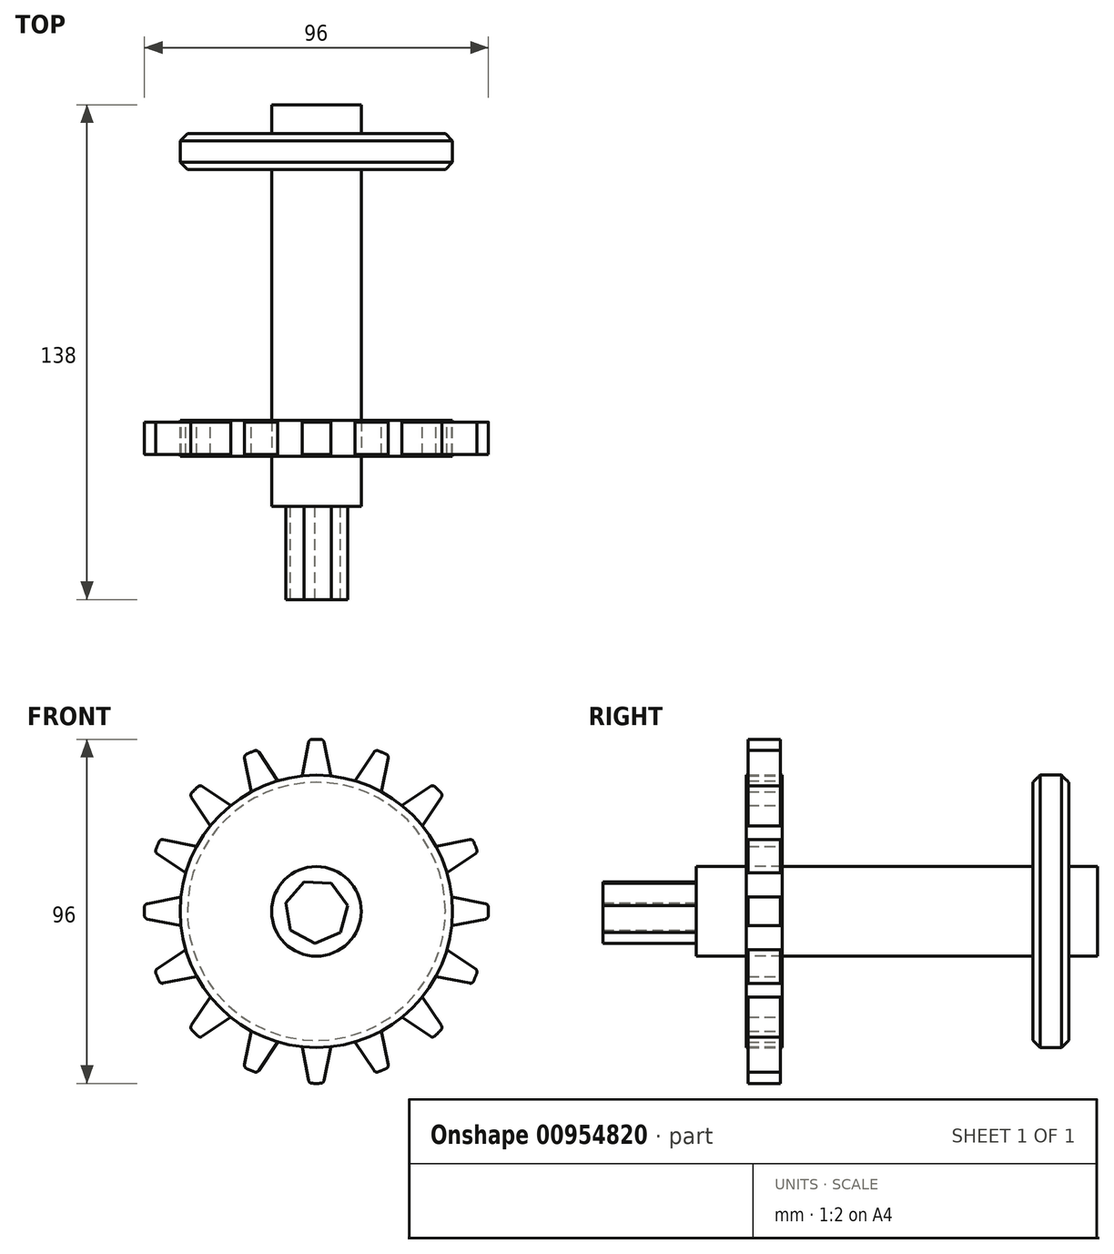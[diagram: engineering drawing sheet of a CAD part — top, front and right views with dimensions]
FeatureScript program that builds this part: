
annotation { "Feature Type Name" : "Feature", "Feature Type Description" : "" }
export const myFeature = defineFeature(function(context is Context, id is Id, definition is map)
    precondition{}
    {
        {
            var Q0;
            Q0=qCreatedBy(makeId("Front.planeOp"),FACE);
            var sketch = newSketch(context, id + "F0", { "sketchPlane" : qUnion([Q0])});
            skCircle(sketch, "E0", {"center": v(0, 0) * mm, "radius": 38 * mm});
            skSolve(sketch);
        }
        {
            var Q0;
            Q0=qSketchRegion(id+"F0",true);
            extrude(context, id + "F1", {"entities" : qUnion([Q0]), "depth" : 10 * mm, "offsetDistance" : 25 * mm});
        }
        {
            var Q0;
            Q0=qCreatedBy(makeId("Front.planeOp"),FACE);
            var Q1;
            Q1=makeQuery(id+"F1.opExtrude","CAP_FACE",FACE,{"disambiguationData":[OSD([sQuery(id+"F0.wireOp",EDGE,"E0")])],"isStart":false});
            cPlane(context, id + "F2", {"entities" : qUnion([Q0, Q1]), "cplaneType" : CPlaneType.MID_PLANE, "offset" : 25 * mm, "width" : 150 * mm, "height" : 150 * mm});
        }
        {
            var Q0;
            Q0=qCreatedBy(id+"F2.planeOp",FACE);
            var sketch = newSketch(context, id + "F3", { "sketchPlane" : qUnion([Q0])});
            skLineSegment(sketch, "E1", {"start": v(-37.79, -4) * mm, "end": v(-37.79, 4) * mm});
            skPoint(sketch, "E2.end.orphan", {"position": v(30.14, 4) * mm});
            skPoint(sketch, "E2.start.orphan", {"position": v(29.89, 0) * mm});
            skLineSegment(sketch, "E3", {"start": v(-37.79, 4) * mm, "end": v(-47.96, 2) * mm});
            skLineSegment(sketch, "E4", {"start": v(-37.79, -4) * mm, "end": v(-47.96, -2) * mm});
            skArc(sketch, "E5", {"start": v(-47.96, 2) * mm, "mid": v(-48, 0) * mm, "end": v(-47.96, -2) * mm, "construction": true});
            skArc(sketch, "E6", {"start": v(-47.96, 2) * mm, "mid": v(-48, 0) * mm, "end": v(-47.96, -2) * mm});
            skSolve(sketch);
        }
        {
            var Q0;
            Q0=makeQuery(id+"F3.imprint","IMPRINT",FACE,{"disambiguationData":[TD([[makeQuery(id+"F3.imprint","IMPRINT",EDGE,{"derivedFrom":sQuery(id+"F3.wireOp",EDGE,"E1")}),1.0]])]});
            extrude(context, id + "F4", {"entities" : qUnion([Q0]), "operationType" : NewBodyOperationType.ADD, "depth" : 9 * mm, "offsetDistance" : 25 * mm, "symmetric" : true});
        }
        {
            var Q0;
            Q0=makeQuery(id+"F4.opExtrude","SWEPT_EDGE",EDGE,{"disambiguationData":[OSD([sQuery(id+"F3.wireOp",EDGE,"E4"),sQuery(id+"F3.wireOp",EDGE,"E6")])]});
            var Q1;
            Q1=makeQuery(id+"F4.opExtrude","SWEPT_EDGE",EDGE,{"disambiguationData":[OSD([sQuery(id+"F3.wireOp",EDGE,"E3"),sQuery(id+"F3.wireOp",EDGE,"E6")])]});
            fillet(context, id + "F5", {"entities" : qUnion([Q0, Q1]), "radius" : 1 * mm, "tangentPropagation" : true, "allowEdgeOverflow" : false});
        }
        {
            var Q0;
            Q0=makeQuery(id+"F1.opExtrude","SWEPT_BODY",BODY,{"disambiguationData":[OSD([sQuery(id+"F0.wireOp",EDGE,"E0")])]});
            var Q1;
            Q1=makeQuery(id+"F1.opExtrude","CAP_EDGE",EDGE,{"disambiguationData":[OSD([sQuery(id+"F0.wireOp",EDGE,"E0")])],"isStart":true});
            circularPattern(context, id + "F6", {"entities" : qUnion([Q0]), "axis" : qUnion([Q1]), "angle" : 360 * degree, "instanceCount" : 16, "equalSpace" : true});
        }
        {
            var Q0;
            Q0=makeQuery(id+"F1.opExtrude","CAP_FACE",FACE,{"disambiguationData":[OSD([sQuery(id+"F0.wireOp",EDGE,"E0")])],"isStart":false});
            var sketch = newSketch(context, id + "F7", { "sketchPlane" : qUnion([Q0])});
            skCircle(sketch, "E7", {"center": v(0, 0) * mm, "radius": 12.5 * mm});
            skPoint(sketch, "E8.0.midPoint", {"position": v(7.03, 3.82) * mm});
            skPoint(sketch, "E9.orphan", {"position": v(4.82, 7.88) * mm});
            skPoint(sketch, "E8.0.end.orphan", {"position": v(9.23, -0.24) * mm});
            skSolve(sketch);
        }
        {
            var Q0;
            Q0 = qSketchRegion(id + "F7", true);
            extrude(context, id + "F8", {"entities" : qUnion([Q0]), "oppositeDirection" : true, "depth" : 98 * mm, "offsetDistance" : 25 * mm});
        }
        {
            var Q0;
            Q0=makeQuery(id+"F8.opExtrude","CAP_FACE",FACE,{"disambiguationData":[OSD([sQuery(id+"F7.wireOp",EDGE,"E7")])],"isStart":true});
            extrude(context, id + "F9", {"entities" : qUnion([Q0]), "depth" : 14 * mm, "offsetDistance" : 25 * mm});
        }
        {
            var Q0;
            Q0=makeQuery(id+"F9.opExtrude","CAP_FACE",FACE,{"disambiguationData":[OSD([sQuery(id+"F7.wireOp",EDGE,"E7")])],"isStart":false});
            var sketch = newSketch(context, id + "F10", { "sketchPlane" : qUnion([Q0])});
            skCircle(sketch, "E10.cCircle", {"center": v(0, 0) * mm, "radius": 8 * mm, "construction": true});
            skLineSegment(sketch, "E10.0", {"start": v(4.23, 7.8) * mm, "end": v(8.74, 1.57) * mm});
            skLineSegment(sketch, "E10.1", {"start": v(8.74, 1.57) * mm, "end": v(6.67, -5.86) * mm});
            skLineSegment(sketch, "E10.2", {"start": v(6.67, -5.86) * mm, "end": v(-0.42, -8.87) * mm});
            skLineSegment(sketch, "E10.3", {"start": v(-0.42, -8.87) * mm, "end": v(-7.2, -5.2) * mm});
            skLineSegment(sketch, "E10.4", {"start": v(-7.2, -5.2) * mm, "end": v(-8.55, 2.38) * mm});
            skLineSegment(sketch, "E10.5", {"start": v(-8.55, 2.38) * mm, "end": v(-3.47, 8.17) * mm});
            skLineSegment(sketch, "E10.6", {"start": v(-3.47, 8.17) * mm, "end": v(4.23, 7.8) * mm});
            skPoint(sketch, "E10.0.midPoint", {"position": v(6.48, 4.69) * mm});
            skSolve(sketch);
        }
        {
            var Q0;
            Q0=makeQuery(id+"F10.imprint","IMPRINT",FACE,{"disambiguationData":[TD([[makeQuery(id+"F10.imprint","IMPRINT",EDGE,{"derivedFrom":sQuery(id+"F10.wireOp",EDGE,"E10.0")}),-1.0]])]});
            extrude(context, id + "F11", {"entities" : qUnion([Q0]), "operationType" : NewBodyOperationType.ADD, "depth" : 26 * mm, "offsetDistance" : 25 * mm});
        }
        {
            var Q0;
            Q0=makeQuery(id+"F8.opExtrude","CAP_FACE",FACE,{"disambiguationData":[OSD([sQuery(id+"F7.wireOp",EDGE,"E7")])],"isStart":false});
            cPlane(context, id + "F12", {"entities" : qUnion([Q0]), "cplaneType" : CPlaneType.OFFSET, "offset" : 13 * mm, "oppositeDirection" : true, "width" : 150 * mm, "height" : 150 * mm});
        }
        {
            var Q0;
            Q0=qCreatedBy(id+"F12.planeOp",FACE);
            var sketch = newSketch(context, id + "F13", { "sketchPlane" : qUnion([Q0])});
            skCircle(sketch, "E11", {"center": v(0, 0) * mm, "radius": 38 * mm});
            skSolve(sketch);
        }
        {
            var Q0;
            Q0=makeQuery(id+"F13.imprint","IMPRINT",FACE,{"disambiguationData":[TD([[makeQuery(id+"F13.imprint","IMPRINT",EDGE,{"derivedFrom":sQuery(id+"F13.wireOp",EDGE,"E11")}),1.0]])]});
            extrude(context, id + "F14", {"entities" : qUnion([Q0]), "operationType" : NewBodyOperationType.ADD, "depth" : 10 * mm, "offsetDistance" : 25 * mm, "symmetric" : true});
        }
        {
            var Q0;
            Q0=makeQuery(id+"F14.opExtrude","CAP_EDGE",EDGE,{"disambiguationData":[OSD([sQuery(id+"F13.wireOp",EDGE,"E11")])],"isStart":false});
            var Q1;
            Q1=makeQuery(id+"F14.opExtrude","CAP_EDGE",EDGE,{"disambiguationData":[OSD([sQuery(id+"F13.wireOp",EDGE,"E11")])],"isStart":true});
            chamfer(context, id + "F15", {"entities" : qUnion([Q0, Q1]), "width" : 2 * mm, "tangentPropagation" : true});
        }
    });
